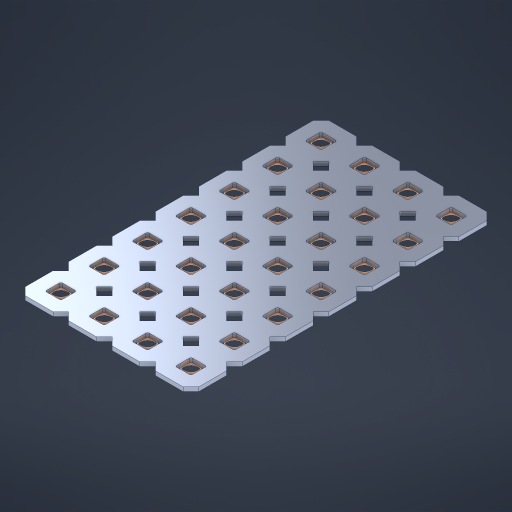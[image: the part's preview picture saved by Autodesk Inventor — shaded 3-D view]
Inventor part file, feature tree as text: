
AUTODESK INVENTOR PART (.ipt)
format: ipt  version: 2023 (Build 270158000, 158)  size: 582,144 bytes
history: native  units: in
note: dims shown in document units (in); Inventor stores cm internally (conversion verified against a paired STEP export)
features: other x29, extrude x27, sketch x2, pattern_linear x1
ambient origin geometry x8: Origin, YZ Plane, XZ Plane, XY Plane, X Axis, Y Axis, Z Axis, Center Point
bodies: Solid1 (feature_tree), Body (feature_tree)
feature tree (59):
  pattern_linear  "Rectangular Pattern1"  Spacing1=0.09in  [1 undecoded]
  sketch  "Sketch1"  dims[d1=0.5in]
  sketch  "Sketch2"  dims[d2=0.182in d3=0.09in d4=0.09in d5=0.09in d6=0.09in d7=0.09in d8=0.09in d9=0.09in d10=0.09in d11=0.02in d13=0.0in d14=0.172in d15=0.0625in d16=0.0in d19=0.5in d22=0.5in]
  other  "Srf1"
  other  "Srf126"
  other  "Srf127"
  other  "Srf128"
  other  "Srf129"
  other  "Srf130"
  other  "Srf131"
  other  "Srf268"
  other  "Srf269"
  other  "Srf270"
  other  "Srf271"
  other  "Srf272"
  other  "Srf273"
  other  "Srf274"
  other  "Srf293"
  other  "Srf294"
  other  "Srf295"
  other  "Srf296"
  other  "Srf297"
  other  "Srf298"
  other  "Srf299"
  other  "Srf318"
  other  "Srf319"
  other  "Srf320"
  other  "Srf321"
  other  "Srf322"
  other  "Srf323"
  other  "Srf324"
  other  "Circle"
  extrude  "ExtrusionSrf126"  Depth=0.09in
  extrude  "ExtrusionSrf127"  Depth=0.09in
  extrude  "ExtrusionSrf128"  Depth=0.09in
  extrude  "ExtrusionSrf129"  Depth=0.09in
  extrude  "ExtrusionSrf130"  Depth=0.09in
  extrude  "ExtrusionSrf131"  Depth=0.09in
  extrude  "ExtrusionSrf268"  Depth=0.09in
  extrude  "ExtrusionSrf269"  Depth=0.02in
  extrude  "ExtrusionSrf270"  TaperAngle=0.0deg  [1 undecoded]
  extrude  "ExtrusionSrf271"  Depth=0.5in
  extrude  "ExtrusionSrf272"  Depth=0.5in TaperAngle=0.0deg
  extrude  "ExtrusionSrf273"  Depth=0.5in
  extrude  "ExtrusionSrf274"  Depth=0.5in
  extrude  "ExtrusionSrf293"  [1 undecoded]
  extrude  "ExtrusionSrf294"  [1 undecoded]
  extrude  "ExtrusionSrf295"  [1 undecoded]
  extrude  "ExtrusionSrf296"  [1 undecoded]
  extrude  "ExtrusionSrf297"  [1 undecoded]
  extrude  "ExtrusionSrf298"  [1 undecoded]
  extrude  "ExtrusionSrf299"  [1 undecoded]
  extrude  "ExtrusionSrf318"  [1 undecoded]
  extrude  "ExtrusionSrf319"  [1 undecoded]
  extrude  "ExtrusionSrf320"  [1 undecoded]
  extrude  "ExtrusionSrf321"  [1 undecoded]
  extrude  "ExtrusionSrf322"  [1 undecoded]
  extrude  "ExtrusionSrf323"  [1 undecoded]
  extrude  "ExtrusionSrf324"  [1 undecoded]
note: 16 required parameter values undecoded (feature->parameter linkage not recoverable at this tier; creation-order binding heuristic only, values carry confidence <= 0.55)
